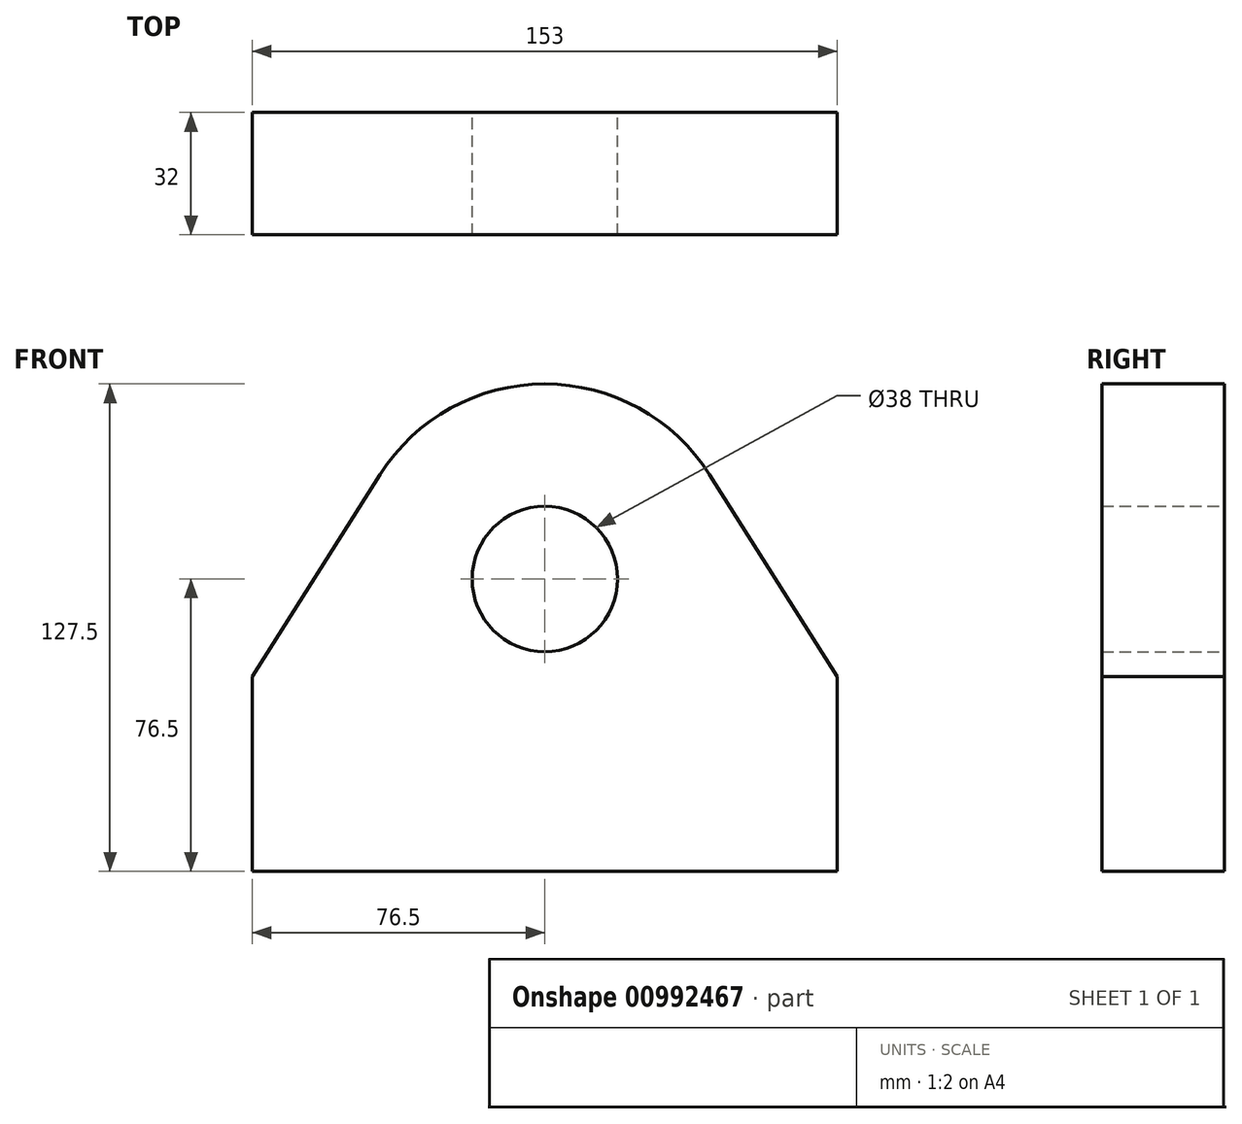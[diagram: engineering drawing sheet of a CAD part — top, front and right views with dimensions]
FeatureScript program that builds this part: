
annotation { "Feature Type Name" : "Feature", "Feature Type Description" : "" }
export const myFeature = defineFeature(function(context is Context, id is Id, definition is map)
    precondition{}
    {
        {
            var Q0;
            Q0=qCreatedBy(makeId("Front.planeOp"),FACE);
            var sketch = newSketch(context, id + "F0", { "sketchPlane" : qUnion([Q0])});
            skArc(sketch, "E0", {"start": v(43.1, 27.28) * mm, "mid": v(0, 51) * mm, "end": v(-43.1, 27.28) * mm});
            skLineSegment(sketch, "E1.bottom", {"start": v(-76.5, -25.5) * mm, "end": v(76.5, -25.5) * mm, "construction": true});
            skLineSegment(sketch, "E1.top", {"start": v(-76.5, -76.5) * mm, "end": v(76.5, -76.5) * mm});
            skLineSegment(sketch, "E1.left", {"start": v(-76.5, -25.5) * mm, "end": v(-76.5, -76.5) * mm});
            skLineSegment(sketch, "E1.right", {"start": v(76.5, -25.5) * mm, "end": v(76.5, -76.5) * mm});
            skLineSegment(sketch, "E2", {"start": v(-60.36, 0) * mm, "end": v(60.36, 0) * mm, "construction": true});
            skLineSegment(sketch, "E3", {"start": v(0, 0) * mm, "end": v(0, -25.5) * mm, "construction": true});
            skLineSegment(sketch, "E4", {"start": v(-76.5, -25.5) * mm, "end": v(-43.1, 27.28) * mm});
            skLineSegment(sketch, "E5", {"start": v(76.5, -25.5) * mm, "end": v(43.1, 27.28) * mm});
            skLineSegment(sketch, "E6.bottom", {"start": v(-19, 0) * mm, "end": v(19, 0) * mm});
            skLineSegment(sketch, "E7", {"start": v(43.1, 27.28) * mm, "end": v(0, 0) * mm, "construction": true});
            skLineSegment(sketch, "E8", {"start": v(43.1, 27.28) * mm, "end": v(-43.1, 27.28) * mm, "construction": true});
            skLineSegment(sketch, "E9", {"start": v(0, 0) * mm, "end": v(0, 27.28) * mm, "construction": true});
            skLineSegment(sketch, "E10", {"start": v(0, 27.28) * mm, "end": v(0, 51) * mm, "construction": true});
            skLineSegment(sketch, "E11", {"start": v(-43.1, 27.28) * mm, "end": v(0, 0) * mm, "construction": true});
            skLineSegment(sketch, "E12", {"start": v(-43.1, 27.28) * mm, "end": v(-43.1, 0) * mm, "construction": true});
            skCircle(sketch, "E13", {"center": v(0, 0) * mm, "radius": 19 * mm});
            skSolve(sketch);
        }
        {
            var Q0;
            Q0 = qSketchRegion(id + "F0", true);
            extrude(context, id + "F1", {"entities" : qUnion([Q0]), "endBound" : BoundingType.SYMMETRIC, "depth" : 32 * mm, "offsetDistance" : 25 * mm});
        }
    });
